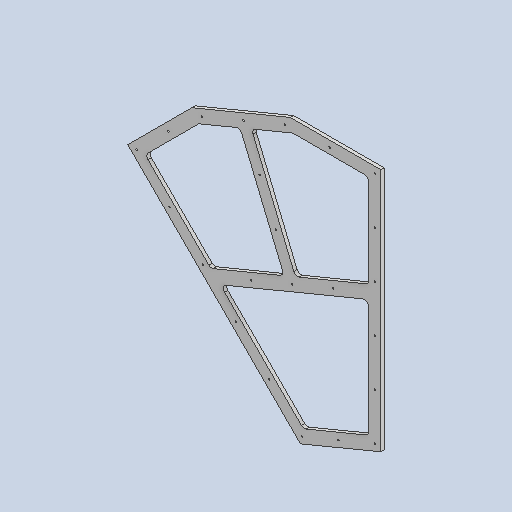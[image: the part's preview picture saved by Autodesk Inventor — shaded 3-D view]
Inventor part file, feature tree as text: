
AUTODESK INVENTOR PART (.ipt)
format: ipt  version: 2025 (Build 290162010, 162A)  size: 212,992 bytes
history: native  units: mm
features: sketch x4, extrude x3, fillet x1
ambient origin geometry x8: Origin, YZ Plane, XZ Plane, XY Plane, X Axis, Y Axis, Z Axis, Center Point
bodies: Solid1 (feature_tree)
feature tree (8):
  extrude  "Extrusion1"  Depth=260.0mm
  extrude  "Extrusion2"  Depth=8.0mm TaperAngle=0.0deg
  fillet  "Fillet1"  Radius=15.0mm
  extrude  "Extrusion4"  Depth=280.0mm
  sketch  "Sketch1"  dims[d0=513.0mm d2=260.0mm]
  sketch  "Sketch2"  dims[d11=30.0mm d12=280.0mm]
  sketch  "Sketch5"  dims[d13=30.0mm d14=30.0mm d15=15.0mm d16=0.0mm d17=0.0mm d18=10.0mm d21=30.0mm d22=30.0mm d23=30.0mm d24=30.0mm d32=15.0mm d33=15.0mm d34=15.0mm d35=4.0mm d37=103.33mm d38=103.33mm d41=60.0mm d43=114.2572mm d44=10.0mm d46=10.0mm d49=108.5mm d50=110.0mm d51=110.0mm d52=10.0mm d53=0.0mm]
  sketch  "Sketch Rectangular Pattern1"  dims[d3=635.0mm d5=8.0mm d6=0.0mm d10=15.0mm]
